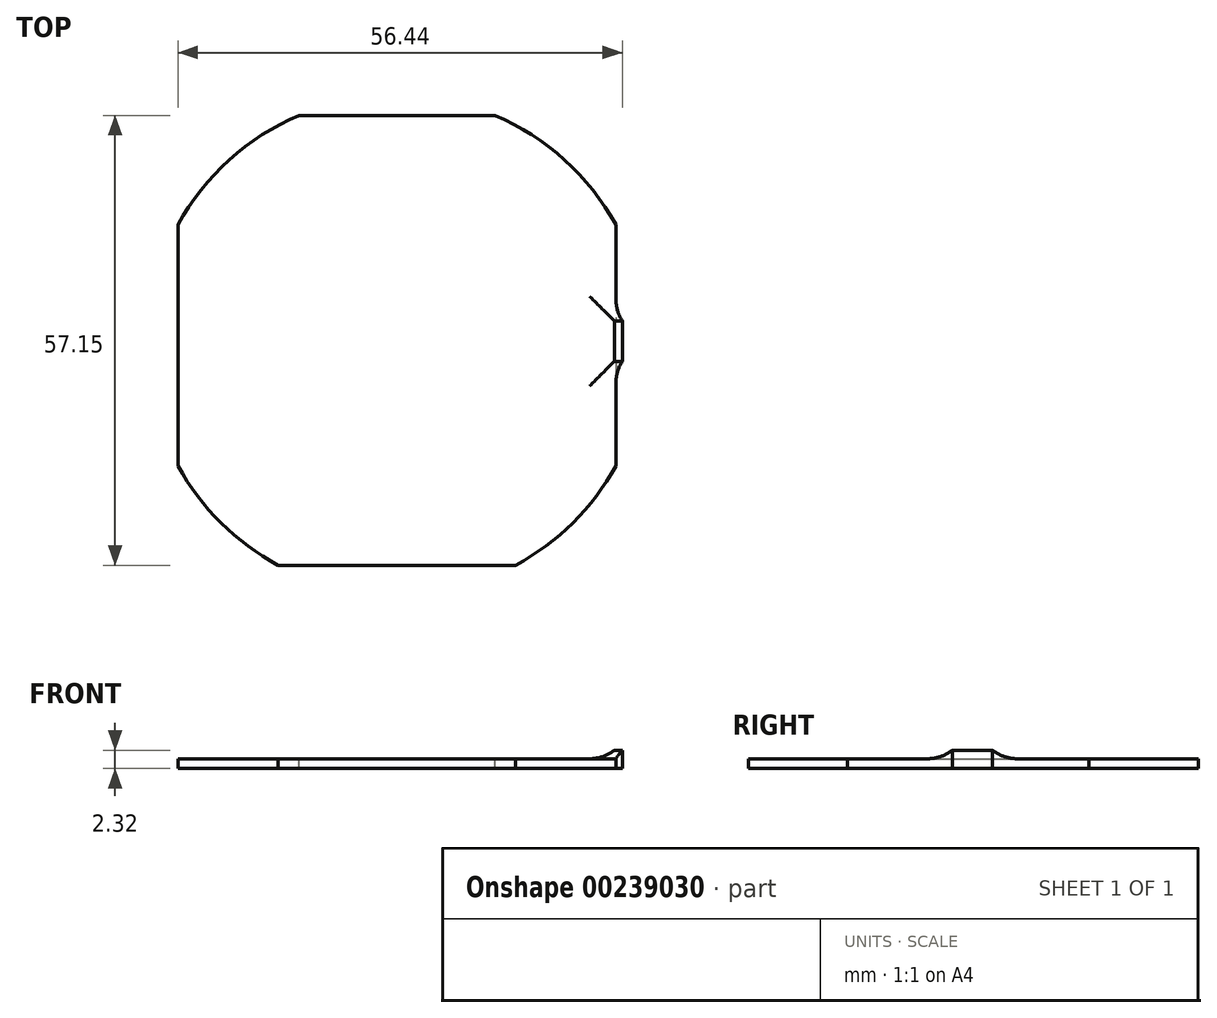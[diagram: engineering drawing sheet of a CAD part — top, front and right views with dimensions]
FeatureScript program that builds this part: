
annotation { "Feature Type Name" : "Feature", "Feature Type Description" : "" }
export const myFeature = defineFeature(function(context is Context, id is Id, definition is map)
    precondition{}
    {
        {
            var Q0;
            Q0=qCreatedBy(makeId("Right.planeOp"),FACE);
            var sketch = newSketch(context, id + "F0", { "sketchPlane" : qUnion([Q0])});
            skLineSegment(sketch, "E0.bottom", {"start": v(-27.94, 0.62) * mm, "end": v(27.94, 0.62) * mm});
            skLineSegment(sketch, "E0.top", {"start": v(-27.94, -0.62) * mm, "end": v(27.94, -0.62) * mm});
            skLineSegment(sketch, "E0.left", {"start": v(-27.94, 0.62) * mm, "end": v(-27.94, -0.62) * mm});
            skLineSegment(sketch, "E0.right", {"start": v(27.94, 0.62) * mm, "end": v(27.94, -0.62) * mm});
            skSolve(sketch);
        }
        {
            var Q0;
            Q0 = qSketchRegion(id + "F0", true);
            extrude(context, id + "F1", {"entities" : qUnion([Q0]), "depth" : 43.43 * mm, "hasSecondDirection" : true, "secondDirectionOppositeDirection" : true, "secondDirectionDepth" : 12.2 * mm});
        }
        {
            var Q0;
            Q0=makeQuery(id+"F1.opExtrude","CAP_FACE",FACE,{"disambiguationData":[OSD([sQuery(id+"F0.wireOp",EDGE,"E0.bottom"),sQuery(id+"F0.wireOp",EDGE,"E0.top"),sQuery(id+"F0.wireOp",EDGE,"E0.left"),sQuery(id+"F0.wireOp",EDGE,"E0.right")])],"isStart":false});
            var sketch = newSketch(context, id + "F2", { "sketchPlane" : qUnion([Q0])});
            skLineSegment(sketch, "E1.bottom", {"start": v(-2.03, 1.7) * mm, "end": v(3.09, 1.7) * mm});
            skLineSegment(sketch, "E1.top", {"start": v(-2.03, -0.62) * mm, "end": v(3.09, -0.62) * mm});
            skLineSegment(sketch, "E1.left", {"start": v(-2.03, 1.7) * mm, "end": v(-2.03, -0.62) * mm});
            skLineSegment(sketch, "E1.right", {"start": v(3.09, 1.7) * mm, "end": v(3.09, -0.62) * mm});
            skSolve(sketch);
        }
        {
            var Q0;
            {var subQ0=sQuery(id+"F2.wireOp",EDGE,"E1.bottom");Q0=makeQuery(id+"F2.imprint","IMPRINT",FACE,{"disambiguationData":[TD([[makeQuery(id+"F2.imprint","IMPRINT",EDGE,{"derivedFrom":subQ0}),-1.0]])]});}
            var Q1;
            {var subQ0=sQuery(id+"F2.wireOp",EDGE,"E1.top");Q1=makeQuery(id+"F2.imprint","IMPRINT",FACE,{"disambiguationData":[TD([[makeQuery(id+"F2.imprint","IMPRINT",EDGE,{"derivedFrom":subQ0}),1.0]])]});}
            extrude(context, id + "F3", {"entities" : qUnion([Q0, Q1]), "operationType" : NewBodyOperationType.ADD, "depth" : 0.81 * mm, "hasSecondDirection" : true, "secondDirectionOppositeDirection" : true, "secondDirectionDepth" : 0.2 * mm});
        }
        {
            var Q0;
            Q0=makeQuery(id+"F1.opExtrude","SWEPT_FACE",FACE,{"disambiguationData":[OSD([sQuery(id+"F0.wireOp",EDGE,"E0.right")])]});
            extrude(context, id + "F4", {"entities" : qUnion([Q0]), "operationType" : NewBodyOperationType.ADD, "depth" : 1.27 * mm});
        }
        {
            var Q0;
            {var subQ0=sQuery(id+"F0.wireOp",EDGE,"E0.bottom");Q0=makeQuery(id+"F4.boolean.opBoolean","MERGE",FACE,{"derivedFrom":[makeQuery(id+"F1.opExtrude","SWEPT_FACE",FACE,{"disambiguationData":[OSD([subQ0])]}),makeQuery(id+"F4.opExtrude","SWEPT_FACE",FACE,{"disambiguationData":[OSD([subQ0,sQuery(id+"F0.wireOp",EDGE,"E0.right")])]})]});}
            var sketch = newSketch(context, id + "F5", { "sketchPlane" : qUnion([Q0])});
            skCircle(sketch, "E2", {"center": v(15.62, 0) * mm, "radius": 31.75 * mm});
            skPoint(sketch, "E2.centerSnap0", {"position": v(15.62, 29.21) * mm});
            skSolve(sketch);
        }
        {
            var Q0;
            {var subQ0=sQuery(id+"F5.wireOp",EDGE,"E2");var subQ1=makeQuery(id+"F4.opExtrude","CAP_EDGE",EDGE,{"disambiguationData":[OSD([sQuery(id+"F0.wireOp",EDGE,"E0.bottom"),sQuery(id+"F0.wireOp",EDGE,"E0.right")])],"isStart":false});var subQ2=makeQuery(id+"F5.imprint","INTERSECT",VERTEX,{"disambiguationData":[OD(0.0)],"derivedFrom":[subQ1,subQ0]});Q0=makeQuery(id+"F5.imprint","IMPRINT",FACE,{"disambiguationData":[TD([[makeQuery(id+"F5.imprint","IMPRINT",EDGE,{"disambiguationData":[TD([[subQ2,-1.0]])],"derivedFrom":subQ0}),1.0]])]});}
            var Q1;
            {var subQ0=sQuery(id+"F5.wireOp",EDGE,"E2");var subQ1=sQuery(id+"F0.wireOp",EDGE,"E0.right");var subQ2=sQuery(id+"F0.wireOp",EDGE,"E0.bottom");var subQ3=makeQuery(id+"F4.boolean.opBoolean","MERGE",EDGE,{"derivedFrom":[makeQuery(id+"F1.opExtrude","CAP_EDGE",EDGE,{"disambiguationData":[OSD([subQ2])],"isStart":true}),makeQuery(id+"F4.opExtrude","SWEPT_EDGE",EDGE,{"disambiguationData":[OSD([subQ2,subQ1]),TDD([makeQuery(id+"F1.opExtrude","CAP_VERTEX",VERTEX,{"disambiguationData":[OSD([subQ2,subQ1])],"isStart":true})])]})]});var subQ4=makeQuery(id+"F5.imprint","INTERSECT",VERTEX,{"disambiguationData":[OD(0.0)],"derivedFrom":[subQ3,subQ0]});Q1=makeQuery(id+"F5.imprint","IMPRINT",FACE,{"disambiguationData":[TD([[makeQuery(id+"F5.imprint","IMPRINT",EDGE,{"disambiguationData":[TD([[subQ4,-1.0]])],"derivedFrom":subQ0}),1.0]])]});}
            var Q2;
            {var subQ0=sQuery(id+"F5.wireOp",EDGE,"E2");var subQ1=makeQuery(id+"F1.opExtrude","SWEPT_EDGE",EDGE,{"disambiguationData":[OSD([sQuery(id+"F0.wireOp",EDGE,"E0.bottom"),sQuery(id+"F0.wireOp",EDGE,"E0.left")])]});var subQ2=makeQuery(id+"F5.imprint","INTERSECT",VERTEX,{"disambiguationData":[OD(0.0)],"derivedFrom":[subQ1,subQ0]});Q2=makeQuery(id+"F5.imprint","IMPRINT",FACE,{"disambiguationData":[TD([[makeQuery(id+"F5.imprint","IMPRINT",EDGE,{"disambiguationData":[TD([[subQ2,-1.0]])],"derivedFrom":subQ0}),1.0]])]});}
            var Q3;
            {var subQ1=sQuery(id+"F0.wireOp",EDGE,"E0.right");var subQ2=sQuery(id+"F0.wireOp",EDGE,"E0.bottom");var subQ3=sQuery(id+"F2.wireOp",EDGE,"E1.right");var subQ4=sQuery(id+"F2.wireOp",EDGE,"E1.left");var subQ5=makeQuery(id+"F3.opExtrude","CAP_FACE",FACE,{"disambiguationData":[OSD([sQuery(id+"F2.wireOp",EDGE,"E1.bottom"),sQuery(id+"F2.wireOp",EDGE,"E1.top"),subQ4,subQ3])],"isStart":true});var subQ6=sQuery(id+"F0.wireOp",EDGE,"E0.left");var subQ7=makeQuery(id+"F1.opExtrude","CAP_FACE",FACE,{"disambiguationData":[OSD([subQ2,sQuery(id+"F0.wireOp",EDGE,"E0.top"),subQ6,subQ1])],"isStart":false});var subQ8=makeQuery(id+"F1.opExtrude","SWEPT_FACE",FACE,{"disambiguationData":[OSD([subQ2])]});var subQ9=makeQuery(id+"F3.opExtrude","SWEPT_FACE",FACE,{"disambiguationData":[OSD([subQ3])]});var subQ10=makeQuery(id+"F1.opExtrude","CAP_EDGE",EDGE,{"disambiguationData":[OSD([subQ2])],"isStart":false});var subQ13=makeQuery(id+"F3.opExtrude","SWEPT_FACE",FACE,{"disambiguationData":[OSD([subQ4])]});var subQ16=makeQuery(id+"F3.boolean.opBoolean","SPLIT",EDGE,{"disambiguationData":[TD([subQ8,subQ7,subQ5,subQ13,subQ9])],"derivedFrom":subQ10});Q3=makeQuery(id+"F5.imprint","IMPRINT",FACE,{"disambiguationData":[TD([[makeQuery(id+"F5.imprint","IMPRINT",EDGE,{"derivedFrom":subQ16}),-1.0]])]});}
            var Q4;
            {var subQ0=sQuery(id+"F5.wireOp",EDGE,"E2");var subQ1=sQuery(id+"F0.wireOp",EDGE,"E0.right");var subQ2=sQuery(id+"F0.wireOp",EDGE,"E0.bottom");var subQ3=makeQuery(id+"F4.opExtrude","CAP_EDGE",EDGE,{"disambiguationData":[OSD([subQ2,subQ1])],"isStart":false});var subQ4=makeQuery(id+"F5.imprint","INTERSECT",VERTEX,{"disambiguationData":[OD(0.0)],"derivedFrom":[subQ3,subQ0]});Q4=makeQuery(id+"F5.imprint","IMPRINT",FACE,{"disambiguationData":[TD([[makeQuery(id+"F5.imprint","IMPRINT",EDGE,{"disambiguationData":[TD([[subQ4,1.0]])],"derivedFrom":subQ0}),-1.0]])]});}
            var Q5;
            {var subQ0=sQuery(id+"F5.wireOp",EDGE,"E2");var subQ1=sQuery(id+"F0.wireOp",EDGE,"E0.left");var subQ2=sQuery(id+"F0.wireOp",EDGE,"E0.bottom");var subQ3=makeQuery(id+"F1.opExtrude","SWEPT_EDGE",EDGE,{"disambiguationData":[OSD([subQ2,subQ1])]});var subQ4=makeQuery(id+"F5.imprint","INTERSECT",VERTEX,{"disambiguationData":[OD(1.0)],"derivedFrom":[subQ3,subQ0]});Q5=makeQuery(id+"F5.imprint","IMPRINT",FACE,{"disambiguationData":[TD([[makeQuery(id+"F5.imprint","IMPRINT",EDGE,{"disambiguationData":[TD([[subQ4,-1.0]])],"derivedFrom":subQ0}),-1.0]])]});}
            var Q6;
            {var subQ0=sQuery(id+"F5.wireOp",EDGE,"E2");var subQ2=sQuery(id+"F0.wireOp",EDGE,"E0.bottom");var subQ5=makeQuery(id+"F1.opExtrude","SWEPT_EDGE",EDGE,{"disambiguationData":[OSD([subQ2,sQuery(id+"F0.wireOp",EDGE,"E0.left")])]});var subQ6=makeQuery(id+"F5.imprint","INTERSECT",VERTEX,{"disambiguationData":[OD(0.0)],"derivedFrom":[subQ5,subQ0]});Q6=makeQuery(id+"F5.imprint","IMPRINT",FACE,{"disambiguationData":[TD([[makeQuery(id+"F5.imprint","IMPRINT",EDGE,{"disambiguationData":[TD([[subQ6,1.0]])],"derivedFrom":subQ0}),-1.0]])]});}
            var Q7;
            {var subQ0=sQuery(id+"F5.wireOp",EDGE,"E2");var subQ1=sQuery(id+"F0.wireOp",EDGE,"E0.right");var subQ2=sQuery(id+"F0.wireOp",EDGE,"E0.bottom");var subQ3=makeQuery(id+"F4.opExtrude","CAP_EDGE",EDGE,{"disambiguationData":[OSD([subQ2,subQ1])],"isStart":false});var subQ4=makeQuery(id+"F5.imprint","INTERSECT",VERTEX,{"disambiguationData":[OD(1.0)],"derivedFrom":[subQ3,subQ0]});Q7=makeQuery(id+"F5.imprint","IMPRINT",FACE,{"disambiguationData":[TD([[makeQuery(id+"F5.imprint","IMPRINT",EDGE,{"disambiguationData":[TD([[subQ4,-1.0]])],"derivedFrom":subQ0}),-1.0]])]});}
            extrude(context, id + "F6", {"entities" : qUnion([Q0, Q1, Q2, Q3, Q4, Q5, Q6, Q7]), "operationType" : NewBodyOperationType.REMOVE, "oppositeDirection" : true, "depth" : 25.4 * mm});
        }
        {
            var Q0;
            Q0=makeQuery(id+"F6.boolean.opBoolean","COPY",FACE,{"derivedFrom":makeQuery(id+"F6.opExtrude","CAP_FACE",FACE,{"disambiguationData":[OSD([sQuery(id+"F0.wireOp",EDGE,"E0.bottom"),sQuery(id+"F0.wireOp",EDGE,"E0.right"),sQuery(id+"F2.wireOp",EDGE,"E1.bottom"),sQuery(id+"F2.wireOp",EDGE,"E1.top"),sQuery(id+"F2.wireOp",EDGE,"E1.left"),sQuery(id+"F2.wireOp",EDGE,"E1.right"),sQuery(id+"F5.wireOp",EDGE,"E2")])],"isStart":true})});
            extrude(context, id + "F7", {"entities" : qUnion([Q0]), "operationType" : NewBodyOperationType.ADD, "depth" : 1.22 * mm});
        }
        {
            var Q0;
            {var subQ0=sQuery(id+"F0.wireOp",EDGE,"E0.bottom");var subQ1=sQuery(id+"F0.wireOp",EDGE,"E0.left");var subQ2=makeQuery(id+"F3.boolean.opBoolean","SPLIT",EDGE,{"disambiguationData":[TD([makeQuery(id+"F1.opExtrude","SWEPT_FACE",FACE,{"disambiguationData":[OSD([subQ1])]})])],"derivedFrom":makeQuery(id+"F1.opExtrude","CAP_EDGE",EDGE,{"disambiguationData":[OSD([subQ0])],"isStart":false})});var subQ3=makeQuery(id+"F1.opExtrude","SWEPT_EDGE",EDGE,{"disambiguationData":[OSD([subQ0,subQ1])]});var subQ5=sQuery(id+"F5.wireOp",EDGE,"E2");var subQ6=makeQuery(id+"F5.imprint","INTERSECT",VERTEX,{"derivedFrom":[subQ2,subQ5]});var subQ7=makeQuery(id+"F5.imprint","INTERSECT",VERTEX,{"disambiguationData":[OD(1.0)],"derivedFrom":[subQ3,subQ5]});Q0=makeQuery(id+"F6.boolean.opBoolean","COPY",EDGE,{"derivedFrom":makeQuery(id+"F6.opExtrude","SWEPT_EDGE",EDGE,{"disambiguationData":[OSD([subQ0,subQ1,subQ5]),TDD([subQ7]),ownerDisambiguation([makeQuery(id+"F6.opExtrude","SWEPT_BODY",BODY,{"disambiguationData":[OSD([subQ0,subQ1,subQ5]),TDD([makeQuery(id+"F5.imprint","IMPRINT",EDGE,{"disambiguationData":[TD([[subQ7,-1.0]])],"derivedFrom":subQ5}),makeQuery(id+"F5.imprint","IMPRINT",EDGE,{"disambiguationData":[TD([[subQ7,1.0]])],"derivedFrom":subQ3}),makeQuery(id+"F5.imprint","IMPRINT",EDGE,{"disambiguationData":[TD([[subQ6,1.0]])],"derivedFrom":subQ2})])]})])]})});}
            var Q1;
            {var subQ0=sQuery(id+"F0.wireOp",EDGE,"E0.bottom");var subQ1=sQuery(id+"F0.wireOp",EDGE,"E0.left");var subQ2=makeQuery(id+"F3.boolean.opBoolean","SPLIT",EDGE,{"disambiguationData":[TD([makeQuery(id+"F1.opExtrude","SWEPT_FACE",FACE,{"disambiguationData":[OSD([subQ1])]})])],"derivedFrom":makeQuery(id+"F1.opExtrude","CAP_EDGE",EDGE,{"disambiguationData":[OSD([subQ0])],"isStart":false})});var subQ3=makeQuery(id+"F1.opExtrude","SWEPT_EDGE",EDGE,{"disambiguationData":[OSD([subQ0,subQ1])]});var subQ5=sQuery(id+"F5.wireOp",EDGE,"E2");var subQ6=makeQuery(id+"F5.imprint","INTERSECT",VERTEX,{"derivedFrom":[subQ2,subQ5]});var subQ7=makeQuery(id+"F5.imprint","INTERSECT",VERTEX,{"disambiguationData":[OD(1.0)],"derivedFrom":[subQ3,subQ5]});Q1=makeQuery(id+"F6.boolean.opBoolean","COPY",EDGE,{"derivedFrom":makeQuery(id+"F6.opExtrude","SWEPT_EDGE",EDGE,{"disambiguationData":[OSD([subQ0,subQ5]),ownerDisambiguation([makeQuery(id+"F6.opExtrude","SWEPT_BODY",BODY,{"disambiguationData":[OSD([subQ0,subQ1,subQ5]),TDD([makeQuery(id+"F5.imprint","IMPRINT",EDGE,{"disambiguationData":[TD([[subQ7,-1.0]])],"derivedFrom":subQ5}),makeQuery(id+"F5.imprint","IMPRINT",EDGE,{"disambiguationData":[TD([[subQ7,1.0]])],"derivedFrom":subQ3}),makeQuery(id+"F5.imprint","IMPRINT",EDGE,{"disambiguationData":[TD([[subQ6,1.0]])],"derivedFrom":subQ2})])]})])]})});}
            var Q2;
            {var subQ0=sQuery(id+"F0.wireOp",EDGE,"E0.right");var subQ1=sQuery(id+"F0.wireOp",EDGE,"E0.bottom");var subQ2=makeQuery(id+"F4.boolean.opBoolean","MERGE",EDGE,{"derivedFrom":[makeQuery(id+"F3.boolean.opBoolean","SPLIT",EDGE,{"disambiguationData":[TD([makeQuery(id+"F1.opExtrude","SWEPT_FACE",FACE,{"disambiguationData":[OSD([subQ0])]})])],"derivedFrom":makeQuery(id+"F1.opExtrude","CAP_EDGE",EDGE,{"disambiguationData":[OSD([subQ1])],"isStart":false})}),makeQuery(id+"F4.opExtrude","SWEPT_EDGE",EDGE,{"disambiguationData":[OSD([subQ1,subQ0]),TDD([makeQuery(id+"F1.opExtrude","CAP_VERTEX",VERTEX,{"disambiguationData":[OSD([subQ1,subQ0])],"isStart":false})])]})]});var subQ3=makeQuery(id+"F4.opExtrude","CAP_EDGE",EDGE,{"disambiguationData":[OSD([subQ1,subQ0])],"isStart":false});var subQ5=sQuery(id+"F5.wireOp",EDGE,"E2");var subQ6=makeQuery(id+"F5.imprint","INTERSECT",VERTEX,{"derivedFrom":[subQ2,subQ5]});var subQ7=makeQuery(id+"F5.imprint","INTERSECT",VERTEX,{"disambiguationData":[OD(0.0)],"derivedFrom":[subQ3,subQ5]});Q2=makeQuery(id+"F6.boolean.opBoolean","COPY",EDGE,{"derivedFrom":makeQuery(id+"F6.opExtrude","SWEPT_EDGE",EDGE,{"disambiguationData":[OSD([subQ1,subQ0,subQ5]),TDD([subQ6]),ownerDisambiguation([makeQuery(id+"F6.opExtrude","SWEPT_BODY",BODY,{"disambiguationData":[OSD([subQ1,subQ0,subQ5]),TDD([makeQuery(id+"F5.imprint","IMPRINT",EDGE,{"disambiguationData":[TD([[subQ7,1.0]])],"derivedFrom":subQ5}),makeQuery(id+"F5.imprint","IMPRINT",EDGE,{"disambiguationData":[TD([[subQ7,1.0]])],"derivedFrom":subQ3}),makeQuery(id+"F5.imprint","IMPRINT",EDGE,{"disambiguationData":[TD([[subQ6,-1.0]])],"derivedFrom":subQ2})])]})])]})});}
            var Q3;
            {var subQ0=sQuery(id+"F0.wireOp",EDGE,"E0.right");var subQ1=sQuery(id+"F0.wireOp",EDGE,"E0.bottom");var subQ2=makeQuery(id+"F4.boolean.opBoolean","MERGE",EDGE,{"derivedFrom":[makeQuery(id+"F3.boolean.opBoolean","SPLIT",EDGE,{"disambiguationData":[TD([makeQuery(id+"F1.opExtrude","SWEPT_FACE",FACE,{"disambiguationData":[OSD([subQ0])]})])],"derivedFrom":makeQuery(id+"F1.opExtrude","CAP_EDGE",EDGE,{"disambiguationData":[OSD([subQ1])],"isStart":false})}),makeQuery(id+"F4.opExtrude","SWEPT_EDGE",EDGE,{"disambiguationData":[OSD([subQ1,subQ0]),TDD([makeQuery(id+"F1.opExtrude","CAP_VERTEX",VERTEX,{"disambiguationData":[OSD([subQ1,subQ0])],"isStart":false})])]})]});var subQ3=makeQuery(id+"F4.opExtrude","CAP_EDGE",EDGE,{"disambiguationData":[OSD([subQ1,subQ0])],"isStart":false});var subQ5=sQuery(id+"F5.wireOp",EDGE,"E2");var subQ6=makeQuery(id+"F5.imprint","INTERSECT",VERTEX,{"derivedFrom":[subQ2,subQ5]});var subQ7=makeQuery(id+"F5.imprint","INTERSECT",VERTEX,{"disambiguationData":[OD(0.0)],"derivedFrom":[subQ3,subQ5]});Q3=makeQuery(id+"F6.boolean.opBoolean","COPY",EDGE,{"derivedFrom":makeQuery(id+"F6.opExtrude","SWEPT_EDGE",EDGE,{"disambiguationData":[OSD([subQ1,subQ0,subQ5]),TDD([subQ7]),ownerDisambiguation([makeQuery(id+"F6.opExtrude","SWEPT_BODY",BODY,{"disambiguationData":[OSD([subQ1,subQ0,subQ5]),TDD([makeQuery(id+"F5.imprint","IMPRINT",EDGE,{"disambiguationData":[TD([[subQ7,1.0]])],"derivedFrom":subQ5}),makeQuery(id+"F5.imprint","IMPRINT",EDGE,{"disambiguationData":[TD([[subQ7,1.0]])],"derivedFrom":subQ3}),makeQuery(id+"F5.imprint","IMPRINT",EDGE,{"disambiguationData":[TD([[subQ6,-1.0]])],"derivedFrom":subQ2})])]})])]})});}
            var Q4;
            {var subQ0=sQuery(id+"F0.wireOp",EDGE,"E0.right");var subQ1=sQuery(id+"F0.wireOp",EDGE,"E0.bottom");var subQ2=makeQuery(id+"F4.boolean.opBoolean","MERGE",EDGE,{"derivedFrom":[makeQuery(id+"F1.opExtrude","CAP_EDGE",EDGE,{"disambiguationData":[OSD([subQ1])],"isStart":true}),makeQuery(id+"F4.opExtrude","SWEPT_EDGE",EDGE,{"disambiguationData":[OSD([subQ1,subQ0]),TDD([makeQuery(id+"F1.opExtrude","CAP_VERTEX",VERTEX,{"disambiguationData":[OSD([subQ1,subQ0])],"isStart":true})])]})]});var subQ3=makeQuery(id+"F4.opExtrude","CAP_EDGE",EDGE,{"disambiguationData":[OSD([subQ1,subQ0])],"isStart":false});var subQ5=sQuery(id+"F5.wireOp",EDGE,"E2");var subQ6=makeQuery(id+"F5.imprint","INTERSECT",VERTEX,{"disambiguationData":[OD(0.0)],"derivedFrom":[subQ2,subQ5]});var subQ7=makeQuery(id+"F5.imprint","INTERSECT",VERTEX,{"disambiguationData":[OD(1.0)],"derivedFrom":[subQ3,subQ5]});Q4=makeQuery(id+"F6.boolean.opBoolean","COPY",EDGE,{"derivedFrom":makeQuery(id+"F6.opExtrude","SWEPT_EDGE",EDGE,{"disambiguationData":[OSD([subQ1,subQ0,subQ5]),TDD([subQ7]),ownerDisambiguation([makeQuery(id+"F6.opExtrude","SWEPT_BODY",BODY,{"disambiguationData":[OSD([subQ1,subQ0,subQ5]),TDD([makeQuery(id+"F5.imprint","IMPRINT",EDGE,{"disambiguationData":[TD([[subQ7,-1.0]])],"derivedFrom":subQ5}),makeQuery(id+"F5.imprint","IMPRINT",EDGE,{"disambiguationData":[TD([[subQ7,-1.0]])],"derivedFrom":subQ3}),makeQuery(id+"F5.imprint","IMPRINT",EDGE,{"disambiguationData":[TD([[subQ6,-1.0]])],"derivedFrom":subQ2})])]})])]})});}
            var Q5;
            {var subQ0=sQuery(id+"F0.wireOp",EDGE,"E0.right");var subQ1=sQuery(id+"F0.wireOp",EDGE,"E0.bottom");var subQ2=makeQuery(id+"F4.boolean.opBoolean","MERGE",EDGE,{"derivedFrom":[makeQuery(id+"F1.opExtrude","CAP_EDGE",EDGE,{"disambiguationData":[OSD([subQ1])],"isStart":true}),makeQuery(id+"F4.opExtrude","SWEPT_EDGE",EDGE,{"disambiguationData":[OSD([subQ1,subQ0]),TDD([makeQuery(id+"F1.opExtrude","CAP_VERTEX",VERTEX,{"disambiguationData":[OSD([subQ1,subQ0])],"isStart":true})])]})]});var subQ3=makeQuery(id+"F4.opExtrude","CAP_EDGE",EDGE,{"disambiguationData":[OSD([subQ1,subQ0])],"isStart":false});var subQ5=sQuery(id+"F5.wireOp",EDGE,"E2");var subQ6=makeQuery(id+"F5.imprint","INTERSECT",VERTEX,{"disambiguationData":[OD(0.0)],"derivedFrom":[subQ2,subQ5]});var subQ7=makeQuery(id+"F5.imprint","INTERSECT",VERTEX,{"disambiguationData":[OD(1.0)],"derivedFrom":[subQ3,subQ5]});Q5=makeQuery(id+"F6.boolean.opBoolean","COPY",EDGE,{"derivedFrom":makeQuery(id+"F6.opExtrude","SWEPT_EDGE",EDGE,{"disambiguationData":[OSD([subQ1,subQ0,subQ5]),TDD([subQ6]),ownerDisambiguation([makeQuery(id+"F6.opExtrude","SWEPT_BODY",BODY,{"disambiguationData":[OSD([subQ1,subQ0,subQ5]),TDD([makeQuery(id+"F5.imprint","IMPRINT",EDGE,{"disambiguationData":[TD([[subQ7,-1.0]])],"derivedFrom":subQ5}),makeQuery(id+"F5.imprint","IMPRINT",EDGE,{"disambiguationData":[TD([[subQ7,-1.0]])],"derivedFrom":subQ3}),makeQuery(id+"F5.imprint","IMPRINT",EDGE,{"disambiguationData":[TD([[subQ6,-1.0]])],"derivedFrom":subQ2})])]})])]})});}
            var Q6;
            {var subQ0=sQuery(id+"F5.wireOp",EDGE,"E2");var subQ1=sQuery(id+"F0.wireOp",EDGE,"E0.right");var subQ2=sQuery(id+"F0.wireOp",EDGE,"E0.bottom");Q6=makeQuery(id+"F6.boolean.opBoolean","COPY",EDGE,{"derivedFrom":makeQuery(id+"F6.opExtrude","SWEPT_EDGE",EDGE,{"disambiguationData":[OSD([subQ2,subQ1,subQ0]),TDD([makeQuery(id+"F5.imprint","INTERSECT",VERTEX,{"disambiguationData":[OD(1.0)],"derivedFrom":[makeQuery(id+"F4.boolean.opBoolean","MERGE",EDGE,{"derivedFrom":[makeQuery(id+"F1.opExtrude","CAP_EDGE",EDGE,{"disambiguationData":[OSD([subQ2])],"isStart":true}),makeQuery(id+"F4.opExtrude","SWEPT_EDGE",EDGE,{"disambiguationData":[OSD([subQ2,subQ1]),TDD([makeQuery(id+"F1.opExtrude","CAP_VERTEX",VERTEX,{"disambiguationData":[OSD([subQ2,subQ1])],"isStart":true})])]})]}),subQ0]})]),ownerDisambiguation([makeQuery(id+"F6.opExtrude","SWEPT_BODY",BODY,{"disambiguationData":[OSD([subQ2,sQuery(id+"F0.wireOp",EDGE,"E0.left"),subQ1,subQ0])]})])]})});}
            var Q7;
            {var subQ0=sQuery(id+"F5.wireOp",EDGE,"E2");var subQ1=sQuery(id+"F0.wireOp",EDGE,"E0.left");var subQ2=sQuery(id+"F0.wireOp",EDGE,"E0.bottom");Q7=makeQuery(id+"F6.boolean.opBoolean","COPY",EDGE,{"derivedFrom":makeQuery(id+"F6.opExtrude","SWEPT_EDGE",EDGE,{"disambiguationData":[OSD([subQ2,subQ1,subQ0]),TDD([makeQuery(id+"F5.imprint","INTERSECT",VERTEX,{"disambiguationData":[OD(0.0)],"derivedFrom":[makeQuery(id+"F1.opExtrude","SWEPT_EDGE",EDGE,{"disambiguationData":[OSD([subQ2,subQ1])]}),subQ0]})]),ownerDisambiguation([makeQuery(id+"F6.opExtrude","SWEPT_BODY",BODY,{"disambiguationData":[OSD([subQ2,subQ1,sQuery(id+"F0.wireOp",EDGE,"E0.right"),subQ0])]})])]})});}
            var Q8;
            {var subQ0=sQuery(id+"F2.wireOp",EDGE,"E1.right");var subQ1=sQuery(id+"F2.wireOp",EDGE,"E1.left");var subQ2=sQuery(id+"F2.wireOp",EDGE,"E1.top");var subQ3=sQuery(id+"F2.wireOp",EDGE,"E1.bottom");var subQ4=makeQuery(id+"F3.opExtrude","CAP_FACE",FACE,{"disambiguationData":[OSD([subQ3,subQ2,subQ1,subQ0])],"isStart":true});var subQ5=sQuery(id+"F0.wireOp",EDGE,"E0.bottom");Q8=makeQuery(id+"F6.boolean.opBoolean","MERGE",EDGE,{"disambiguationData":[topologyDisambiguationEdgeConnected([subQ4])],"derivedFrom":[makeQuery(id+"F3.boolean.opBoolean","INTERSECT",EDGE,{"derivedFrom":[makeQuery(id+"F1.opExtrude","SWEPT_FACE",FACE,{"disambiguationData":[OSD([subQ5])]}),subQ4]}),makeQuery(id+"F6.opExtrude","CAP_EDGE",EDGE,{"disambiguationData":[OSD([subQ5,subQ3,subQ2,subQ1,subQ0])],"isStart":true})]});}
            var Q9;
            {var subQ0=sQuery(id+"F0.wireOp",EDGE,"E0.right");var subQ1=sQuery(id+"F0.wireOp",EDGE,"E0.bottom");var subQ2=makeQuery(id+"F1.opExtrude","CAP_FACE",FACE,{"disambiguationData":[OSD([subQ1,sQuery(id+"F0.wireOp",EDGE,"E0.top"),sQuery(id+"F0.wireOp",EDGE,"E0.left"),subQ0])],"isStart":false});var subQ3=sQuery(id+"F2.wireOp",EDGE,"E1.right");var subQ4=makeQuery(id+"F3.opExtrude","SWEPT_FACE",FACE,{"disambiguationData":[OSD([subQ3])]});Q9=makeQuery(id+"F7.boolean.opBoolean","SPLIT",EDGE,{"disambiguationData":[topologyDisambiguationEdgeConnected([subQ4])],"derivedFrom":makeQuery(id+"F6.boolean.opBoolean","MERGE",EDGE,{"derivedFrom":[makeQuery(id+"F3.boolean.opBoolean","INTERSECT",EDGE,{"derivedFrom":[subQ2,subQ4]}),makeQuery(id+"F6.opExtrude","SWEPT_EDGE",EDGE,{"disambiguationData":[OSD([subQ1,subQ0,subQ3])]})]})});}
            var Q10;
            {var subQ0=sQuery(id+"F0.wireOp",EDGE,"E0.bottom");var subQ1=makeQuery(id+"F1.opExtrude","CAP_FACE",FACE,{"disambiguationData":[OSD([subQ0,sQuery(id+"F0.wireOp",EDGE,"E0.top"),sQuery(id+"F0.wireOp",EDGE,"E0.left"),sQuery(id+"F0.wireOp",EDGE,"E0.right")])],"isStart":false});var subQ2=sQuery(id+"F2.wireOp",EDGE,"E1.left");var subQ3=makeQuery(id+"F3.opExtrude","SWEPT_FACE",FACE,{"disambiguationData":[OSD([subQ2])]});Q10=makeQuery(id+"F7.boolean.opBoolean","SPLIT",EDGE,{"disambiguationData":[topologyDisambiguationEdgeConnected([subQ3])],"derivedFrom":makeQuery(id+"F6.boolean.opBoolean","MERGE",EDGE,{"derivedFrom":[makeQuery(id+"F3.boolean.opBoolean","INTERSECT",EDGE,{"derivedFrom":[subQ1,subQ3]}),makeQuery(id+"F6.opExtrude","SWEPT_EDGE",EDGE,{"disambiguationData":[OSD([subQ0,subQ2])]})]})});}
            var Q11;
            {var subQ0=sQuery(id+"F2.wireOp",EDGE,"E1.right");var subQ1=makeQuery(id+"F3.opExtrude","SWEPT_FACE",FACE,{"disambiguationData":[OSD([subQ0])]});var subQ2=sQuery(id+"F0.wireOp",EDGE,"E0.bottom");Q11=makeQuery(id+"F6.boolean.opBoolean","MERGE",EDGE,{"disambiguationData":[topologyDisambiguationEdgeConnected([subQ1])],"derivedFrom":[makeQuery(id+"F3.boolean.opBoolean","INTERSECT",EDGE,{"derivedFrom":[makeQuery(id+"F1.opExtrude","SWEPT_FACE",FACE,{"disambiguationData":[OSD([subQ2])]}),subQ1]}),makeQuery(id+"F6.opExtrude","CAP_EDGE",EDGE,{"disambiguationData":[OSD([subQ2,subQ0])],"isStart":true})]});}
            var Q12;
            {var subQ0=sQuery(id+"F2.wireOp",EDGE,"E1.left");var subQ1=makeQuery(id+"F3.opExtrude","SWEPT_FACE",FACE,{"disambiguationData":[OSD([subQ0])]});var subQ2=sQuery(id+"F0.wireOp",EDGE,"E0.bottom");Q12=makeQuery(id+"F6.boolean.opBoolean","MERGE",EDGE,{"disambiguationData":[topologyDisambiguationEdgeConnected([subQ1])],"derivedFrom":[makeQuery(id+"F3.boolean.opBoolean","INTERSECT",EDGE,{"derivedFrom":[makeQuery(id+"F1.opExtrude","SWEPT_FACE",FACE,{"disambiguationData":[OSD([subQ2])]}),subQ1]}),makeQuery(id+"F6.opExtrude","CAP_EDGE",EDGE,{"disambiguationData":[OSD([subQ2,subQ0])],"isStart":true})]});}
            fillet(context, id + "F8", {"entities" : qUnion([Q0, Q1, Q2, Q3, Q4, Q5, Q6, Q7, Q8, Q9, Q10, Q11, Q12]), "radius" : 5.08 * mm, "tangentPropagation" : true, "allowEdgeOverflow" : false});
        }
    });
